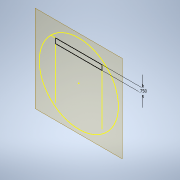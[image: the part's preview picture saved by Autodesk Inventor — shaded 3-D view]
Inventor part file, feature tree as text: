
AUTODESK INVENTOR PART (.ipt)
format: ipt  version: 2021 (Build 250183000, 183)  size: 101,376 bytes
history: native  units: in
note: dims shown in document units (in); Inventor stores cm internally (conversion verified against a paired STEP export)
features: reference x5, other x4, plane x1, extrude x1, sketch x1
ambient origin geometry x8: Origin, YZ Plane, XZ Plane, XY Plane, X Axis, Y Axis, Z Axis, Center Point
bodies: Solid1 (feature_tree)
feature tree (12):
  plane  "Work Plane1"
  extrude  "Extrusion1"  Depth=4.0in TaperAngle=0.0deg
  sketch  "Sketch1"  dims[d0=0.75in d1=4.0in d2=0.0in]
  reference  "Reference1"
  reference  "Reference2"
  reference  "Reference3"
  reference  "Reference4"
  reference  "Reference5"
  other  "roughDraft-12inchBase.iam"
  other  "base-12-inch-diameter:1"
  other  "sideSupportFor12inchBase:1"
  other  "sideSupportFor12inchBase_MIR:1"
